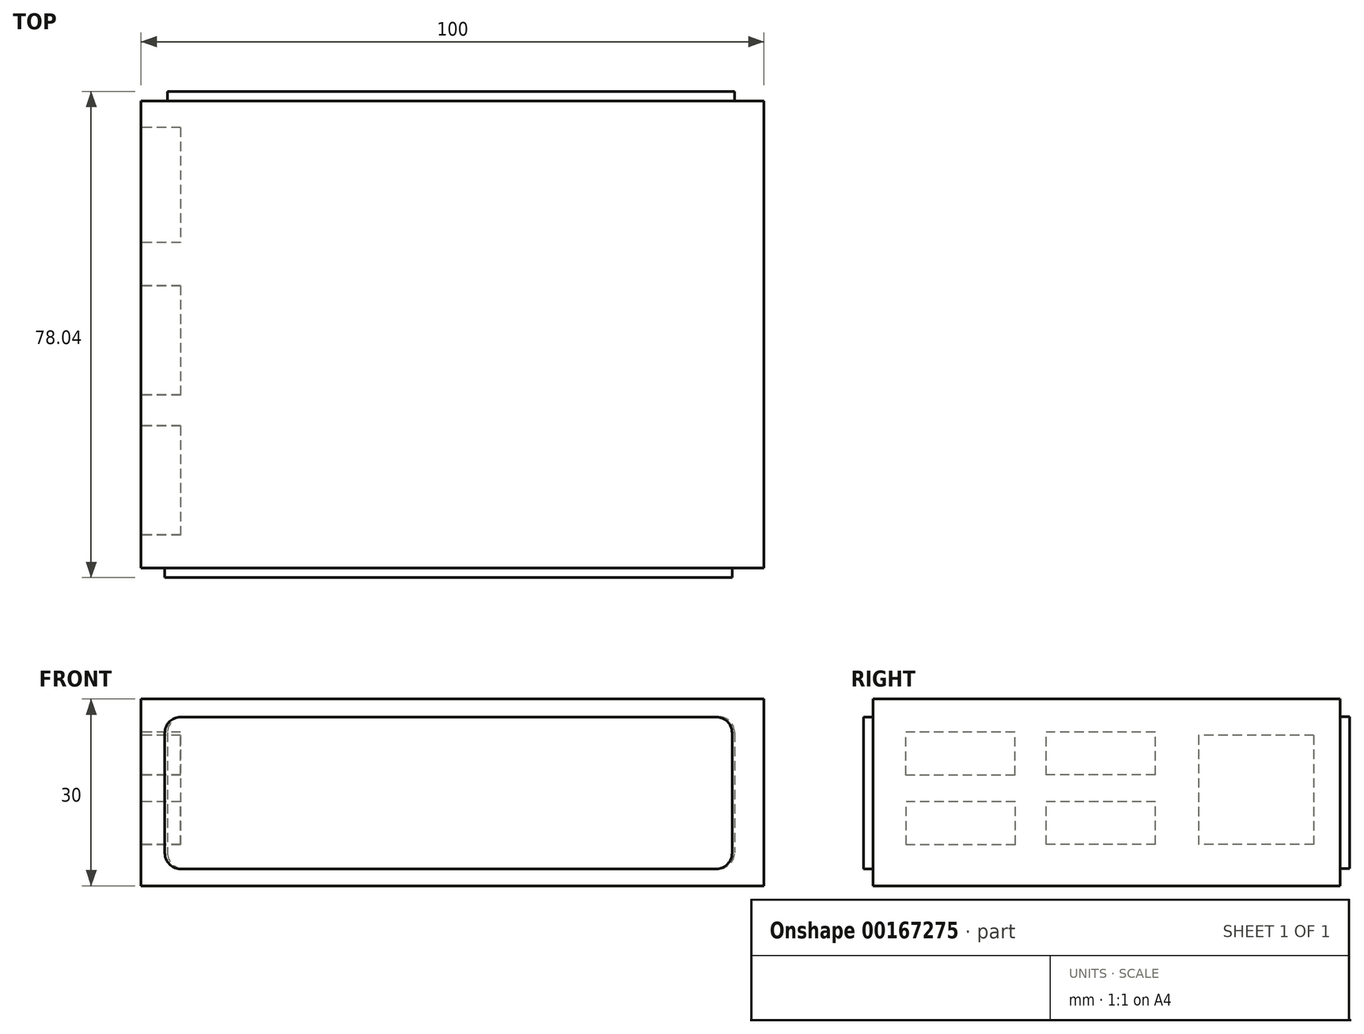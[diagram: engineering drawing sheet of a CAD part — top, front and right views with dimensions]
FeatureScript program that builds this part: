
annotation { "Feature Type Name" : "Feature", "Feature Type Description" : "" }
export const myFeature = defineFeature(function(context is Context, id is Id, definition is map)
    precondition{}
    {
        {
            var Q0;
            Q0=qCreatedBy(makeId("Top.planeOp"),FACE);
            var sketch = newSketch(context, id + "F0", { "sketchPlane" : qUnion([Q0])});
            skLineSegment(sketch, "E0.bottom", {"start": v(-50, 37.5) * mm, "end": v(50, 37.5) * mm});
            skLineSegment(sketch, "E0.top", {"start": v(-50, -37.5) * mm, "end": v(50, -37.5) * mm});
            skLineSegment(sketch, "E0.left", {"start": v(-50, 37.5) * mm, "end": v(-50, -37.5) * mm});
            skLineSegment(sketch, "E0.right", {"start": v(50, 37.5) * mm, "end": v(50, -37.5) * mm});
            skPoint(sketch, "E0.middle", {"position": v(0, 0) * mm});
            skSolve(sketch);
        }
        {
            var Q0;
            Q0=makeQuery(id+"F0.imprint","IMPRINT",FACE,{"disambiguationData":[TD([[makeQuery(id+"F0.imprint","IMPRINT",EDGE,{"derivedFrom":sQuery(id+"F0.wireOp",EDGE,"E0.bottom")}),-1.0]])]});
            extrude(context, id + "F1", {"entities" : qUnion([Q0]), "depth" : 30 * mm});
        }
        {
            var Q0;
            Q0=makeQuery(id+"F1.opExtrude","SWEPT_FACE",FACE,{"disambiguationData":[OSD([sQuery(id+"F0.wireOp",EDGE,"E0.top")])]});
            var sketch = newSketch(context, id + "F2", { "sketchPlane" : qUnion([Q0])});
            skLineSegment(sketch, "E1.bottom", {"start": v(-43.65, 27.1) * mm, "end": v(42.34, 27.1) * mm});
            skLineSegment(sketch, "E1.top", {"start": v(-43.65, 2.7) * mm, "end": v(42.34, 2.7) * mm});
            skLineSegment(sketch, "E1.left", {"start": v(-46.19, 24.57) * mm, "end": v(-46.19, 5.24) * mm});
            skLineSegment(sketch, "E1.right", {"start": v(44.88, 24.57) * mm, "end": v(44.88, 5.24) * mm});
            skPoint(sketch, "E2.visualSharp", {"position": v(-46.19, 27.1) * mm});
            skArc(sketch, "E2.filletArc", {"start": v(-43.65, 27.1) * mm, "mid": v(-45.44, 26.36) * mm, "end": v(-46.19, 24.57) * mm});
            skPoint(sketch, "E3.visualSharp", {"position": v(44.88, 27.1) * mm});
            skArc(sketch, "E3.filletArc", {"start": v(44.88, 24.57) * mm, "mid": v(44.13, 26.36) * mm, "end": v(42.34, 27.1) * mm});
            skPoint(sketch, "E4.visualSharp", {"position": v(-46.19, 2.7) * mm});
            skArc(sketch, "E4.filletArc", {"start": v(-46.19, 5.24) * mm, "mid": v(-45.44, 3.45) * mm, "end": v(-43.65, 2.7) * mm});
            skPoint(sketch, "E5.visualSharp", {"position": v(44.88, 2.7) * mm});
            skArc(sketch, "E5.filletArc", {"start": v(42.34, 2.7) * mm, "mid": v(44.13, 3.45) * mm, "end": v(44.88, 5.24) * mm});
            skSolve(sketch);
        }
        {
            var Q0;
            Q0=makeQuery(id+"F2.imprint","IMPRINT",FACE,{"disambiguationData":[TD([[makeQuery(id+"F2.imprint","IMPRINT",EDGE,{"derivedFrom":sQuery(id+"F2.wireOp",EDGE,"E1.bottom")}),-1.0]])]});
            var Q1;
            Q1=sQuery(id+"F2.wireOp",EDGE,"E1.bottom");
            var Q2;
            Q2=sQuery(id+"F2.wireOp",EDGE,"E2.filletArc");
            var Q3;
            Q3=sQuery(id+"F2.wireOp",EDGE,"E1.left");
            var Q4;
            Q4=sQuery(id+"F2.wireOp",EDGE,"E1.top");
            var Q5;
            Q5=sQuery(id+"F2.wireOp",EDGE,"E4.filletArc");
            extrude(context, id + "F3", {"entities" : qUnion([Q0]), "operationType" : NewBodyOperationType.ADD, "surfaceEntities" : qUnion([Q1, Q2, Q3, Q4, Q5]), "depth" : 1.52 * mm});
        }
        {
            var Q0;
            Q0=makeQuery(id+"F1.opExtrude","SWEPT_FACE",FACE,{"disambiguationData":[OSD([sQuery(id+"F0.wireOp",EDGE,"E0.bottom")])]});
            var sketch = newSketch(context, id + "F4", { "sketchPlane" : qUnion([Q0])});
            skLineSegment(sketch, "E6.bottom", {"start": v(-42.74, 27.15) * mm, "end": v(43.25, 27.15) * mm});
            skLineSegment(sketch, "E6.top", {"start": v(-42.74, 2.75) * mm, "end": v(43.25, 2.75) * mm});
            skLineSegment(sketch, "E6.left", {"start": v(-45.28, 24.61) * mm, "end": v(-45.28, 5.29) * mm});
            skLineSegment(sketch, "E6.right", {"start": v(45.79, 24.61) * mm, "end": v(45.79, 5.29) * mm});
            skPoint(sketch, "E7.visualSharp", {"position": v(-45.28, 27.15) * mm});
            skArc(sketch, "E7.filletArc", {"start": v(-42.74, 27.15) * mm, "mid": v(-44.54, 26.4) * mm, "end": v(-45.28, 24.61) * mm});
            skPoint(sketch, "E8.visualSharp", {"position": v(45.79, 27.15) * mm});
            skArc(sketch, "E8.filletArc", {"start": v(45.79, 24.61) * mm, "mid": v(45.04, 26.4) * mm, "end": v(43.25, 27.15) * mm});
            skPoint(sketch, "E9.visualSharp", {"position": v(-45.28, 2.75) * mm});
            skArc(sketch, "E9.filletArc", {"start": v(-45.28, 5.29) * mm, "mid": v(-44.54, 3.5) * mm, "end": v(-42.74, 2.75) * mm});
            skPoint(sketch, "E10.visualSharp", {"position": v(45.79, 2.75) * mm});
            skArc(sketch, "E10.filletArc", {"start": v(43.25, 2.75) * mm, "mid": v(45.04, 3.5) * mm, "end": v(45.79, 5.29) * mm});
            skSolve(sketch);
        }
        {
            var Q0;
            Q0 = qSketchRegion(id + "F4", true);
            extrude(context, id + "F5", {"entities" : qUnion([Q0]), "operationType" : NewBodyOperationType.ADD, "depth" : 1.52 * mm});
        }
        {
            var Q0;
            Q0=makeQuery(id+"F1.opExtrude","SWEPT_FACE",FACE,{"disambiguationData":[OSD([sQuery(id+"F0.wireOp",EDGE,"E0.left")])]});
            var sketch = newSketch(context, id + "F6", { "sketchPlane" : qUnion([Q0])});
            skLineSegment(sketch, "E11.bottom", {"start": v(-33.25, 24.16) * mm, "end": v(-14.74, 24.16) * mm});
            skLineSegment(sketch, "E11.top", {"start": v(-33.25, 6.63) * mm, "end": v(-14.74, 6.63) * mm});
            skLineSegment(sketch, "E11.left", {"start": v(-33.25, 24.16) * mm, "end": v(-33.25, 6.63) * mm});
            skLineSegment(sketch, "E11.right", {"start": v(-14.74, 24.16) * mm, "end": v(-14.74, 6.63) * mm});
            skLineSegment(sketch, "E12.bottom", {"start": v(-7.86, 6.63) * mm, "end": v(9.66, 6.63) * mm});
            skLineSegment(sketch, "E12.top", {"start": v(-7.86, 13.51) * mm, "end": v(9.66, 13.51) * mm});
            skLineSegment(sketch, "E12.left", {"start": v(-7.86, 6.63) * mm, "end": v(-7.86, 13.51) * mm});
            skLineSegment(sketch, "E12.right", {"start": v(9.66, 6.63) * mm, "end": v(9.66, 13.51) * mm});
            skLineSegment(sketch, "E13.bottom", {"start": v(-7.81, 17.8) * mm, "end": v(9.71, 17.8) * mm});
            skLineSegment(sketch, "E13.top", {"start": v(-7.81, 24.69) * mm, "end": v(9.71, 24.69) * mm});
            skLineSegment(sketch, "E13.left", {"start": v(-7.81, 17.8) * mm, "end": v(-7.81, 24.69) * mm});
            skLineSegment(sketch, "E13.right", {"start": v(9.71, 17.8) * mm, "end": v(9.71, 24.69) * mm});
            skLineSegment(sketch, "E14.bottom", {"start": v(14.65, 6.6) * mm, "end": v(32.18, 6.6) * mm});
            skLineSegment(sketch, "E14.top", {"start": v(14.65, 13.49) * mm, "end": v(32.18, 13.49) * mm});
            skLineSegment(sketch, "E14.left", {"start": v(14.65, 6.6) * mm, "end": v(14.65, 13.49) * mm});
            skLineSegment(sketch, "E14.right", {"start": v(32.18, 6.6) * mm, "end": v(32.18, 13.49) * mm});
            skLineSegment(sketch, "E15.bottom", {"start": v(14.7, 17.78) * mm, "end": v(32.23, 17.78) * mm});
            skLineSegment(sketch, "E15.top", {"start": v(14.7, 24.66) * mm, "end": v(32.23, 24.66) * mm});
            skLineSegment(sketch, "E15.left", {"start": v(14.7, 17.78) * mm, "end": v(14.7, 24.66) * mm});
            skLineSegment(sketch, "E15.right", {"start": v(32.23, 17.78) * mm, "end": v(32.23, 24.66) * mm});
            skSolve(sketch);
        }
        {
            var Q0;
            Q0 = qSketchRegion(id + "F6", true);
            extrude(context, id + "F7", {"entities" : qUnion([Q0]), "operationType" : NewBodyOperationType.REMOVE, "oppositeDirection" : true, "depth" : 6.35 * mm});
        }
    });
